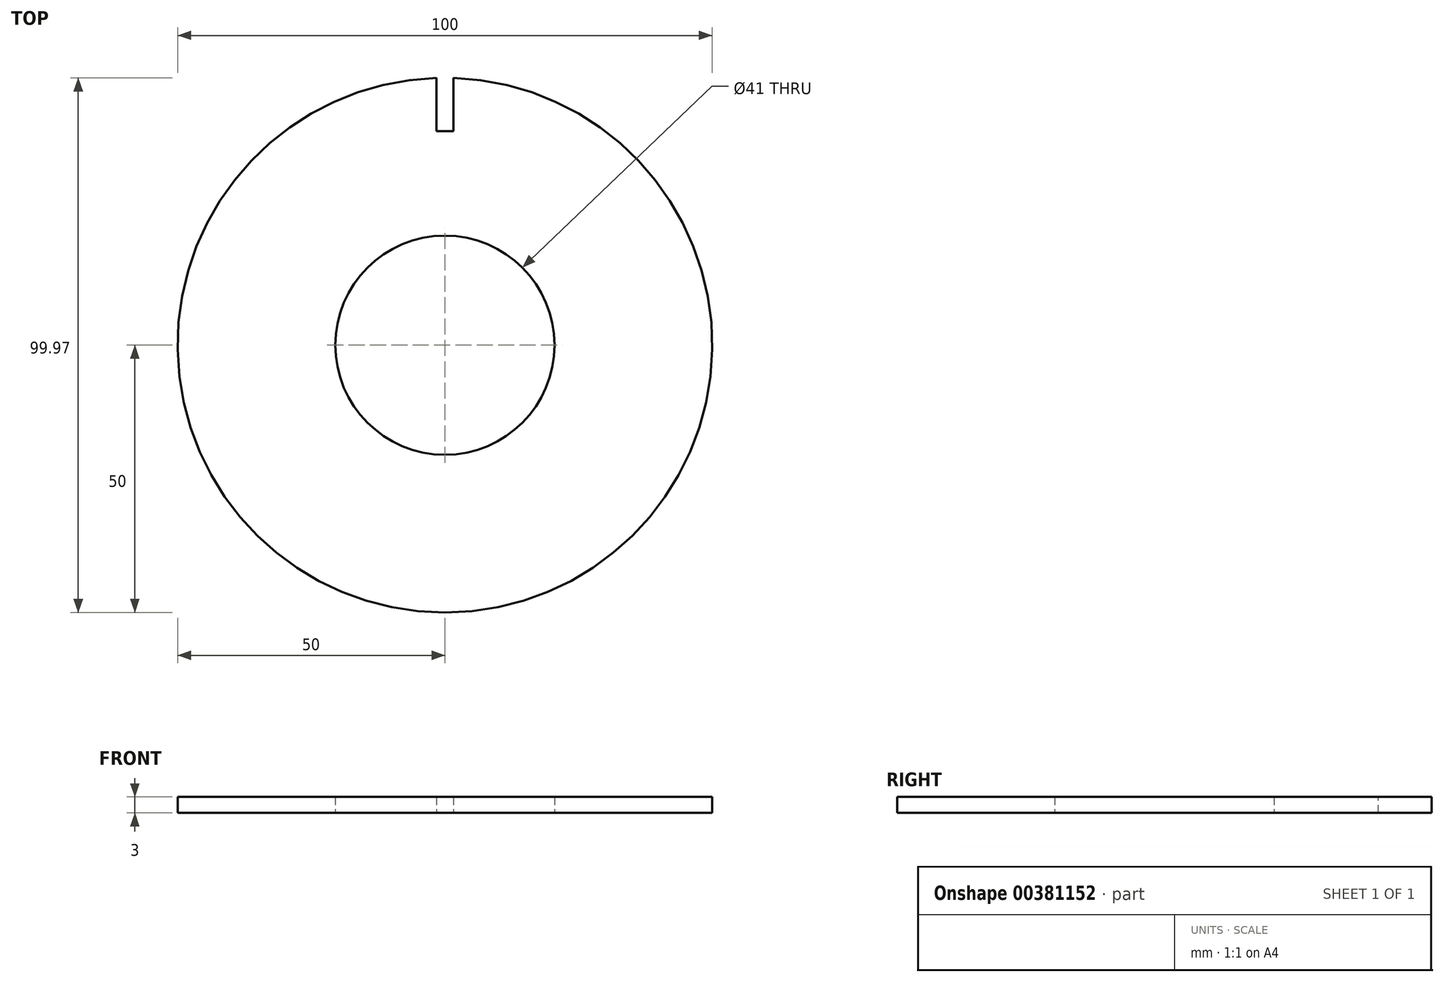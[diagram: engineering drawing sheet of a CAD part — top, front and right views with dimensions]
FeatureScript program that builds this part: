
annotation { "Feature Type Name" : "Feature", "Feature Type Description" : "" }
export const myFeature = defineFeature(function(context is Context, id is Id, definition is map)
    precondition{}
    {
        {
            var Q0;
            Q0=qCreatedBy(makeId("Top.planeOp"),FACE);
            var sketch = newSketch(context, id + "F0", { "sketchPlane" : qUnion([Q0])});
            skCircle(sketch, "E0", {"center": v(0, 0) * mm, "radius": 50 * mm});
            skCircle(sketch, "E1", {"center": v(0, 0) * mm, "radius": 20.5 * mm});
            skSolve(sketch);
        }
        {
            var Q0;
            Q0 = qSketchRegion(id + "F0", true);
            extrude(context, id + "F1", {"entities" : qUnion([Q0]), "depth" : 3 * mm, "offsetDistance" : 25 * mm});
        }
        {
            var Q0;
            Q0=makeQuery(id+"F1.opExtrude","CAP_FACE",FACE,{"disambiguationData":[OSD([sQuery(id+"F0.wireOp",EDGE,"E0"),sQuery(id+"F0.wireOp",EDGE,"E1")])],"isStart":false});
            var sketch = newSketch(context, id + "F2", { "sketchPlane" : qUnion([Q0])});
            skLineSegment(sketch, "E2.bottom", {"start": v(-1.6, 80) * mm, "end": v(1.6, 80) * mm});
            skLineSegment(sketch, "E2.top", {"start": v(-1.6, 40) * mm, "end": v(1.6, 40) * mm});
            skLineSegment(sketch, "E2.left", {"start": v(-1.6, 80) * mm, "end": v(-1.6, 40) * mm});
            skLineSegment(sketch, "E2.right", {"start": v(1.6, 80) * mm, "end": v(1.6, 40) * mm});
            skLineSegment(sketch, "E3", {"start": v(0, 0) * mm, "end": v(0, 51.96) * mm, "construction": true});
            skSolve(sketch);
        }
        {
            var Q0;
            Q0 = qSketchRegion(id + "F2", true);
            extrude(context, id + "F3", {"entities" : qUnion([Q0]), "operationType" : NewBodyOperationType.REMOVE, "oppositeDirection" : true, "depth" : 25 * mm});
        }
    });
